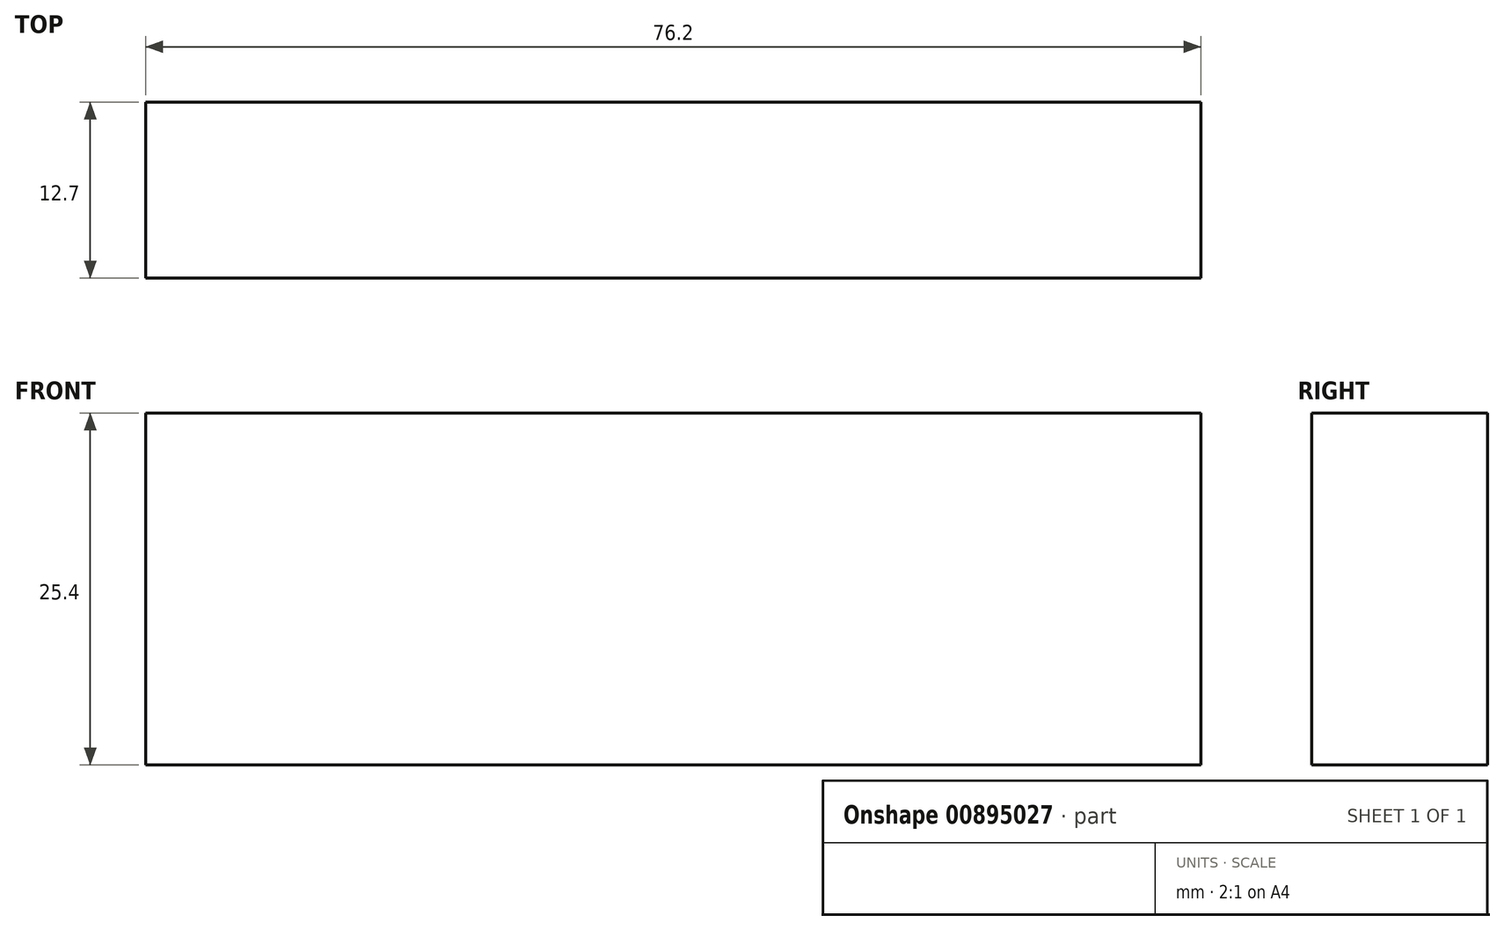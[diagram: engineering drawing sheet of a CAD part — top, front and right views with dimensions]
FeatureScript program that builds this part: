
annotation { "Feature Type Name" : "Feature", "Feature Type Description" : "" }
export const myFeature = defineFeature(function(context is Context, id is Id, definition is map)
    precondition{}
    {
        {
            var Q0;
            Q0=qCreatedBy(makeId("Top.planeOp"),FACE);
            var sketch = newSketch(context, id + "F0", { "sketchPlane" : qUnion([Q0])});
            skLineSegment(sketch, "E0.bottom", {"start": v(-75.8, -13.72) * mm, "end": v(-152, -13.72) * mm});
            skLineSegment(sketch, "E0.top", {"start": v(-75.8, -1.02) * mm, "end": v(-152, -1.02) * mm});
            skLineSegment(sketch, "E0.left", {"start": v(-75.8, -13.72) * mm, "end": v(-75.8, -1.02) * mm});
            skLineSegment(sketch, "E0.right", {"start": v(-152, -13.72) * mm, "end": v(-152, -1.02) * mm});
            skPoint(sketch, "E0.middle", {"position": v(-113.9, -7.37) * mm});
            skSolve(sketch);
        }
        {
            var Q0;
            Q0 = qSketchRegion(id + "F0", true);
            extrude(context, id + "F1", {"entities" : qUnion([Q0]), "depth" : 25.4 * mm, "offsetDistance" : 25.4 * mm});
        }
    });
